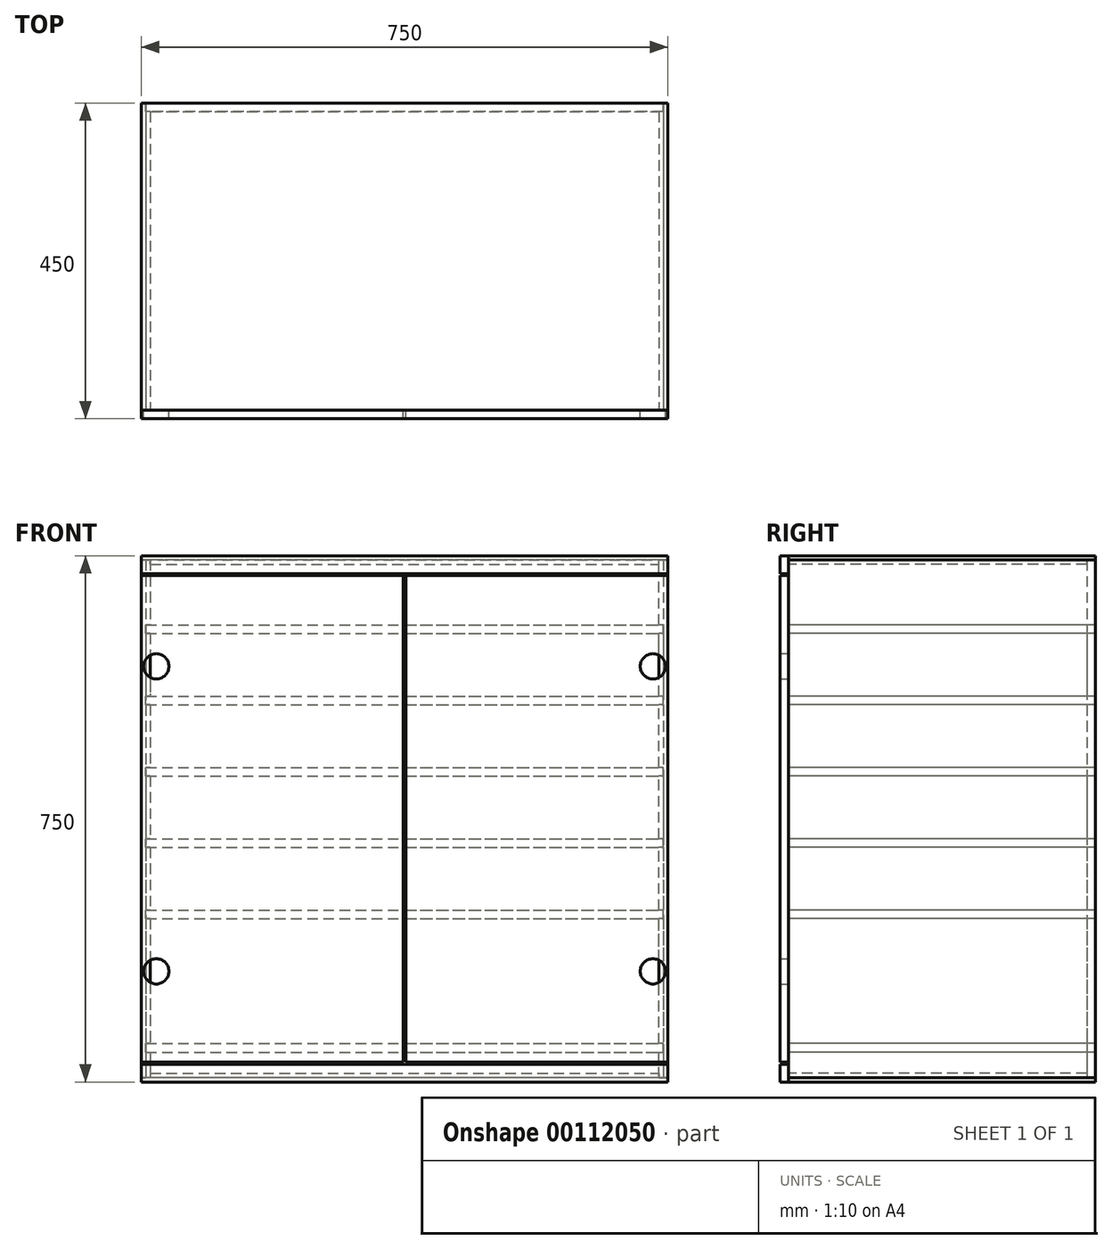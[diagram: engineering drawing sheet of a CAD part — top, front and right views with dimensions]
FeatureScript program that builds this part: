
annotation { "Feature Type Name" : "Feature", "Feature Type Description" : "" }
export const myFeature = defineFeature(function(context is Context, id is Id, definition is map)
    precondition{}
    {
        {
            assignVariable(context, id + "F0", {"name" : "moduleDepth", "anyValue" : 450 * mm});
        }
        {
            assignVariable(context, id + "F1", {"name" : "sideThick", "anyValue" : 12.45 * mm});
        }
        {
            assignVariable(context, id + "F2", {"name" : "backingThick", "anyValue" : getVariable(context, 'sideThick')});
        }
        {
            assignVariable(context, id + "F3", {"name" : "drawerFaceThick", "anyValue" : getVariable(context, 'sideThick')});
        }
        {
            assignVariable(context, id + "F4", {"name" : "drawerCaseDepth", "anyValue" : getVariable(context, 'moduleDepth') - getVariable(context, 'drawerFaceThick')});
        }
        {
            var Q0;
            Q0=qCreatedBy(makeId("Front.planeOp"),FACE);
            var sketch = newSketch(context, id + "F5", { "sketchPlane" : qUnion([Q0])});
            skLineSegment(sketch, "E0.bottom", {"start": v(0, 0) * mm, "end": v(750, 0) * mm});
            skLineSegment(sketch, "E0.top", {"start": v(0, 750) * mm, "end": v(750, 750) * mm});
            skLineSegment(sketch, "E0.left", {"start": v(0, 0) * mm, "end": v(0, 750) * mm});
            skLineSegment(sketch, "E0.right", {"start": v(750, 0) * mm, "end": v(750, 750) * mm});
            skLineSegment(sketch, "E1.bottom", {"start": v(12.45, 12.45) * mm, "end": v(737.55, 12.45) * mm});
            skLineSegment(sketch, "E1.top", {"start": v(12.45, 737.55) * mm, "end": v(737.55, 737.55) * mm});
            skLineSegment(sketch, "E1.left", {"start": v(12.45, 12.45) * mm, "end": v(12.45, 737.55) * mm});
            skLineSegment(sketch, "E1.right", {"start": v(737.55, 12.45) * mm, "end": v(737.55, 737.55) * mm});
            skLineSegment(sketch, "E2", {"start": v(0, 375) * mm, "end": v(750, 375) * mm, "construction": true});
            skLineSegment(sketch, "E3", {"start": v(375, 750) * mm, "end": v(375, 0) * mm, "construction": true});
            skLineSegment(sketch, "E4", {"start": v(12.45, 737.55) * mm, "end": v(12.45, 743.78) * mm});
            skLineSegment(sketch, "E5", {"start": v(12.45, 743.78) * mm, "end": v(0, 743.78) * mm});
            skLineSegment(sketch, "E6.MirrorCS", {"start": v(737.55, 743.78) * mm, "end": v(750, 743.78) * mm});
            skLineSegment(sketch, "E7.MirrorCS", {"start": v(737.55, 737.55) * mm, "end": v(737.55, 743.78) * mm});
            skLineSegment(sketch, "E8.MirrorCS", {"start": v(12.45, 12.45) * mm, "end": v(12.45, 6.22) * mm});
            skLineSegment(sketch, "E9.MirrorCS", {"start": v(737.55, 12.45) * mm, "end": v(737.55, 6.22) * mm});
            skLineSegment(sketch, "E10.MirrorCS", {"start": v(737.55, 6.22) * mm, "end": v(750, 6.22) * mm});
            skLineSegment(sketch, "E11.MirrorCS", {"start": v(12.45, 6.22) * mm, "end": v(0, 6.22) * mm});
            skSolve(sketch);
        }
        {
            var Q0;
            Q0=qCreatedBy(makeId("Front.planeOp"),FACE);
            var sketch = newSketch(context, id + "F6", { "sketchPlane" : qUnion([Q0])});
            skLineSegment(sketch, "E12", {"start": v(6.22, -31.87) * mm, "end": v(6.22, 794) * mm, "construction": true});
            skLineSegment(sketch, "E13", {"start": v(6.22, -31.87) * mm, "end": v(743.78, -31.87) * mm, "construction": true});
            skLineSegment(sketch, "E14", {"start": v(743.78, -31.87) * mm, "end": v(743.78, 794) * mm, "construction": true});
            skLineSegment(sketch, "E15", {"start": v(6.22, 794) * mm, "end": v(743.78, 794) * mm, "construction": true});
            skLineSegment(sketch, "E16.bottom", {"start": v(6.22, 42.45) * mm, "end": v(743.78, 42.45) * mm});
            skLineSegment(sketch, "E16.top", {"start": v(6.22, 54.9) * mm, "end": v(743.78, 54.9) * mm});
            skLineSegment(sketch, "E16.left", {"start": v(6.22, 42.45) * mm, "end": v(6.22, 54.9) * mm});
            skLineSegment(sketch, "E16.right", {"start": v(743.78, 42.45) * mm, "end": v(743.78, 54.9) * mm});
            skLineSegment(sketch, "E17.bottom", {"start": v(6.22, 232.7) * mm, "end": v(743.78, 232.7) * mm});
            skLineSegment(sketch, "E17.top", {"start": v(6.22, 245.14) * mm, "end": v(743.78, 245.14) * mm});
            skLineSegment(sketch, "E17.left", {"start": v(6.22, 232.7) * mm, "end": v(6.22, 245.14) * mm});
            skLineSegment(sketch, "E17.right", {"start": v(743.78, 232.7) * mm, "end": v(743.78, 245.14) * mm});
            skLineSegment(sketch, "E18.0.1.0", {"start": v(6.22, 346.74) * mm, "end": v(743.78, 346.74) * mm});
            skLineSegment(sketch, "E18.0.1.1", {"start": v(6.22, 334.3) * mm, "end": v(743.78, 334.3) * mm});
            skLineSegment(sketch, "E18.0.1.2", {"start": v(743.78, 334.3) * mm, "end": v(743.78, 346.74) * mm});
            skLineSegment(sketch, "E18.0.1.3", {"start": v(6.22, 334.3) * mm, "end": v(6.22, 346.74) * mm});
            skLineSegment(sketch, "E18.0.2.0", {"start": v(6.22, 448.34) * mm, "end": v(743.78, 448.34) * mm});
            skLineSegment(sketch, "E18.0.2.1", {"start": v(6.22, 435.9) * mm, "end": v(743.78, 435.9) * mm});
            skLineSegment(sketch, "E18.0.2.2", {"start": v(743.78, 435.9) * mm, "end": v(743.78, 448.34) * mm});
            skLineSegment(sketch, "E18.0.2.3", {"start": v(6.22, 435.9) * mm, "end": v(6.22, 448.34) * mm});
            skLineSegment(sketch, "E18.0.3.0", {"start": v(6.22, 549.94) * mm, "end": v(743.78, 549.94) * mm});
            skLineSegment(sketch, "E18.0.3.1", {"start": v(6.22, 537.5) * mm, "end": v(743.78, 537.5) * mm});
            skLineSegment(sketch, "E18.0.3.2", {"start": v(743.78, 537.5) * mm, "end": v(743.78, 549.94) * mm});
            skLineSegment(sketch, "E18.0.3.3", {"start": v(6.22, 537.5) * mm, "end": v(6.22, 549.94) * mm});
            skLineSegment(sketch, "E18.0.4.0", {"start": v(6.22, 651.54) * mm, "end": v(743.78, 651.54) * mm});
            skLineSegment(sketch, "E18.0.4.1", {"start": v(6.22, 639.1) * mm, "end": v(743.78, 639.1) * mm});
            skLineSegment(sketch, "E18.0.4.2", {"start": v(743.78, 639.1) * mm, "end": v(743.78, 651.54) * mm});
            skLineSegment(sketch, "E18.0.4.3", {"start": v(6.22, 639.1) * mm, "end": v(6.22, 651.54) * mm});
            skLineSegment(sketch, "E18.direction1", {"start": v(6.22, 232.7) * mm, "end": v(31.22, 232.7) * mm, "construction": true});
            skLineSegment(sketch, "E18.direction2", {"start": v(6.22, 232.7) * mm, "end": v(6.22, 334.3) * mm, "construction": true});
            skSolve(sketch);
        }
        {
            var Q0;
            Q0=qCreatedBy(makeId("Front.planeOp"),FACE);
            var sketch = newSketch(context, id + "F7", { "sketchPlane" : qUnion([Q0])});
            skLineSegment(sketch, "E19.bottom", {"start": v(0, 0) * mm, "end": v(750, 0) * mm});
            skLineSegment(sketch, "E19.top", {"start": v(0, 25.4) * mm, "end": v(750, 25.4) * mm});
            skLineSegment(sketch, "E19.left", {"start": v(0, 0) * mm, "end": v(0, 25.4) * mm});
            skLineSegment(sketch, "E19.right", {"start": v(750, 0) * mm, "end": v(750, 25.4) * mm});
            skLineSegment(sketch, "E20.MirrorCS", {"start": v(0, 750) * mm, "end": v(0, 724.6) * mm});
            skLineSegment(sketch, "E21.MirrorCS", {"start": v(750, 750) * mm, "end": v(750, 724.6) * mm});
            skLineSegment(sketch, "E22.MirrorCS", {"start": v(0, 724.6) * mm, "end": v(750, 724.6) * mm});
            skLineSegment(sketch, "E23.MirrorCS", {"start": v(0, 750) * mm, "end": v(750, 750) * mm});
            skLineSegment(sketch, "E24.bottom", {"start": v(0, 28.4) * mm, "end": v(373, 28.4) * mm});
            skLineSegment(sketch, "E24.top", {"start": v(0, 721.6) * mm, "end": v(373, 721.6) * mm});
            skLineSegment(sketch, "E24.left", {"start": v(0, 28.4) * mm, "end": v(0, 721.6) * mm});
            skLineSegment(sketch, "E24.right", {"start": v(373, 28.4) * mm, "end": v(373, 721.6) * mm});
            skLineSegment(sketch, "E25.MirrorCS", {"start": v(377, 28.4) * mm, "end": v(377, 721.6) * mm});
            skLineSegment(sketch, "E26.MirrorCS", {"start": v(750, 28.4) * mm, "end": v(750, 721.6) * mm});
            skLineSegment(sketch, "E27.MirrorCS", {"start": v(750, 721.6) * mm, "end": v(377, 721.6) * mm});
            skLineSegment(sketch, "E28.MirrorCS", {"start": v(750, 28.4) * mm, "end": v(377, 28.4) * mm});
            skCircle(sketch, "E29", {"center": v(21, 157.66) * mm, "radius": 18 * mm});
            skLineSegment(sketch, "E30", {"start": v(7.58, 145.66) * mm, "end": v(34.42, 145.66) * mm});
            skLineSegment(sketch, "E31", {"start": v(34.42, 145.66) * mm, "end": v(34.42, 169.66) * mm, "construction": true});
            skLineSegment(sketch, "E32", {"start": v(34.42, 169.66) * mm, "end": v(7.58, 169.66) * mm});
            skCircle(sketch, "E33.MirrorC", {"center": v(729, 157.66) * mm, "radius": 18 * mm});
            skLineSegment(sketch, "E34.MirrorCS", {"start": v(715.58, 145.66) * mm, "end": v(715.58, 169.66) * mm, "construction": true});
            skLineSegment(sketch, "E35.MirrorCS", {"start": v(742.42, 145.66) * mm, "end": v(715.58, 145.66) * mm});
            skLineSegment(sketch, "E36.MirrorCS", {"start": v(715.58, 169.66) * mm, "end": v(742.42, 169.66) * mm});
            skLineSegment(sketch, "E37.MirrorCS", {"start": v(34.42, 580.34) * mm, "end": v(7.58, 580.34) * mm});
            skLineSegment(sketch, "E38.MirrorCS", {"start": v(742.42, 604.34) * mm, "end": v(715.58, 604.34) * mm});
            skLineSegment(sketch, "E39.MirrorCS", {"start": v(715.58, 580.34) * mm, "end": v(742.42, 580.34) * mm});
            skLineSegment(sketch, "E40.MirrorCS", {"start": v(7.58, 604.34) * mm, "end": v(34.42, 604.34) * mm});
            skLineSegment(sketch, "E41.MirrorCS", {"start": v(34.42, 604.34) * mm, "end": v(34.42, 580.34) * mm, "construction": true});
            skLineSegment(sketch, "E42.MirrorCS", {"start": v(715.58, 604.34) * mm, "end": v(715.58, 580.34) * mm, "construction": true});
            skCircle(sketch, "E43.MirrorC", {"center": v(729, 592.34) * mm, "radius": 18 * mm});
            skCircle(sketch, "E44.MirrorC", {"center": v(21, 592.34) * mm, "radius": 18 * mm});
            skSolve(sketch);
        }
        {
            var Q0;
            {var subQ1=sQuery(id+"F5.wireOp",EDGE,"E0.top");Q0=makeQuery(id+"F5.imprint","IMPRINT",FACE,{"disambiguationData":[TD([[makeQuery(id+"F5.imprint","IMPRINT",EDGE,{"derivedFrom":subQ1}),-1.0]])]});}
            var Q1;
            {var subQ1=sQuery(id+"F5.wireOp",EDGE,"E0.bottom");Q1=makeQuery(id+"F5.imprint","IMPRINT",FACE,{"disambiguationData":[TD([[makeQuery(id+"F5.imprint","IMPRINT",EDGE,{"derivedFrom":subQ1}),1.0]])]});}
            extrude(context, id + "F8", {"entities" : qUnion([Q0, Q1]), "oppositeDirection" : true, "depth" : getVariable(context, 'drawerCaseDepth')});
        }
        {
            var Q0;
            Q0=makeQuery(id+"F5.imprint","IMPRINT",FACE,{"disambiguationData":[TD([[makeQuery(id+"F5.imprint","IMPRINT",EDGE,{"derivedFrom":sQuery(id+"F5.wireOp",EDGE,"E1.left")}),1.0]])]});
            var Q1;
            Q1=makeQuery(id+"F5.imprint","IMPRINT",FACE,{"disambiguationData":[TD([[makeQuery(id+"F5.imprint","IMPRINT",EDGE,{"derivedFrom":sQuery(id+"F5.wireOp",EDGE,"E1.right")}),-1.0]])]});
            var Q2;
            Q2=makeQuery(id+"F8.opExtrude","CAP_FACE",FACE,{"disambiguationData":[OSD([sQuery(id+"F5.wireOp",EDGE,"E0.top"),sQuery(id+"F5.wireOp",EDGE,"E0.left"),sQuery(id+"F5.wireOp",EDGE,"E0.right"),sQuery(id+"F5.wireOp",EDGE,"E1.top"),sQuery(id+"F5.wireOp",EDGE,"E4"),sQuery(id+"F5.wireOp",EDGE,"E5"),sQuery(id+"F5.wireOp",EDGE,"E6.MirrorCS"),sQuery(id+"F5.wireOp",EDGE,"E7.MirrorCS")])],"isStart":false});
            var Q3;
            Q3=makeQuery(id+"F8.opExtrude","CAP_FACE",FACE,{"disambiguationData":[OSD([sQuery(id+"F5.wireOp",EDGE,"E0.top"),sQuery(id+"F5.wireOp",EDGE,"E0.left"),sQuery(id+"F5.wireOp",EDGE,"E0.right"),sQuery(id+"F5.wireOp",EDGE,"E1.top"),sQuery(id+"F5.wireOp",EDGE,"E4"),sQuery(id+"F5.wireOp",EDGE,"E5"),sQuery(id+"F5.wireOp",EDGE,"E6.MirrorCS"),sQuery(id+"F5.wireOp",EDGE,"E7.MirrorCS")])],"isStart":true});
            extrude(context, id + "F9", {"entities" : qUnion([Q0, Q1]), "endBound" : BoundingType.UP_TO_SURFACE, "oppositeDirection" : true, "endBoundEntityFace" : qUnion([Q2]), "depth" : 25.4 * mm});
        }
        {
            var Q0;
            Q0=makeQuery(id+"F8.opExtrude","CAP_FACE",FACE,{"disambiguationData":[OSD([sQuery(id+"F5.wireOp",EDGE,"E0.top"),sQuery(id+"F5.wireOp",EDGE,"E0.left"),sQuery(id+"F5.wireOp",EDGE,"E0.right"),sQuery(id+"F5.wireOp",EDGE,"E1.top"),sQuery(id+"F5.wireOp",EDGE,"E4"),sQuery(id+"F5.wireOp",EDGE,"E5"),sQuery(id+"F5.wireOp",EDGE,"E6.MirrorCS"),sQuery(id+"F5.wireOp",EDGE,"E7.MirrorCS")])],"isStart":false});
            var sketch = newSketch(context, id + "F10", { "sketchPlane" : qUnion([Q0])});
            skLineSegment(sketch, "E45.bottom", {"start": v(-743.78, 743.78) * mm, "end": v(-6.22, 743.78) * mm});
            skLineSegment(sketch, "E45.top", {"start": v(-743.78, 6.22) * mm, "end": v(-6.22, 6.22) * mm});
            skLineSegment(sketch, "E45.left", {"start": v(-743.78, 743.78) * mm, "end": v(-743.78, 6.22) * mm});
            skLineSegment(sketch, "E45.right", {"start": v(-6.22, 743.78) * mm, "end": v(-6.22, 6.22) * mm});
            skSolve(sketch);
        }
        {
            var Q0;
            Q0=qSketchRegion(id+"F10",true);
            extrude(context, id + "F11", {"entities" : qUnion([Q0]), "oppositeDirection" : true, "depth" : getVariable(context, 'backingThick')});
        }
        {
            var Q0;
            Q0=makeQuery(id+"F11.opExtrude","SWEPT_BODY",BODY,{"disambiguationData":[OSD([sQuery(id+"F10.wireOp",EDGE,"E45.bottom"),sQuery(id+"F10.wireOp",EDGE,"E45.top"),sQuery(id+"F10.wireOp",EDGE,"E45.left"),sQuery(id+"F10.wireOp",EDGE,"E45.right")])]});
            var Q1;
            Q1=makeQuery(id+"F8.opExtrude","SWEPT_BODY",BODY,{"disambiguationData":[OSD([sQuery(id+"F5.wireOp",EDGE,"E0.top"),sQuery(id+"F5.wireOp",EDGE,"E0.left"),sQuery(id+"F5.wireOp",EDGE,"E0.right"),sQuery(id+"F5.wireOp",EDGE,"E1.top"),sQuery(id+"F5.wireOp",EDGE,"E4"),sQuery(id+"F5.wireOp",EDGE,"E5"),sQuery(id+"F5.wireOp",EDGE,"E6.MirrorCS"),sQuery(id+"F5.wireOp",EDGE,"E7.MirrorCS")])]});
            var Q2;
            Q2=makeQuery(id+"F9.opExtrude","SWEPT_BODY",BODY,{"disambiguationData":[OSD([sQuery(id+"F5.wireOp",EDGE,"E0.right"),sQuery(id+"F5.wireOp",EDGE,"E1.right"),sQuery(id+"F5.wireOp",EDGE,"E6.MirrorCS"),sQuery(id+"F5.wireOp",EDGE,"E7.MirrorCS"),sQuery(id+"F5.wireOp",EDGE,"E9.MirrorCS"),sQuery(id+"F5.wireOp",EDGE,"E10.MirrorCS")])]});
            var Q3;
            Q3=makeQuery(id+"F9.opExtrude","SWEPT_BODY",BODY,{"disambiguationData":[OSD([sQuery(id+"F5.wireOp",EDGE,"E0.left"),sQuery(id+"F5.wireOp",EDGE,"E1.left"),sQuery(id+"F5.wireOp",EDGE,"E4"),sQuery(id+"F5.wireOp",EDGE,"E5"),sQuery(id+"F5.wireOp",EDGE,"E8.MirrorCS"),sQuery(id+"F5.wireOp",EDGE,"E11.MirrorCS")])]});
            var Q4;
            Q4=makeQuery(id+"F8.opExtrude","SWEPT_BODY",BODY,{"disambiguationData":[OSD([sQuery(id+"F5.wireOp",EDGE,"E0.bottom"),sQuery(id+"F5.wireOp",EDGE,"E0.left"),sQuery(id+"F5.wireOp",EDGE,"E0.right"),sQuery(id+"F5.wireOp",EDGE,"E1.bottom"),sQuery(id+"F5.wireOp",EDGE,"E8.MirrorCS"),sQuery(id+"F5.wireOp",EDGE,"E9.MirrorCS"),sQuery(id+"F5.wireOp",EDGE,"E10.MirrorCS"),sQuery(id+"F5.wireOp",EDGE,"E11.MirrorCS")])]});
            booleanBodies(context, id + "F12", {"operationType" : BooleanOperationType.SUBTRACTION, "tools" : qUnion([Q0]), "targets" : qUnion([Q1, Q2, Q3, Q4]), "keepTools" : true});
        }
        {
            var Q0;
            Q0 = qSketchRegion(id + "F6", true);
            extrude(context, id + "F13", {"entities" : qUnion([Q0]), "oppositeDirection" : true, "depth" : getVariable(context, 'moduleDepth') - getVariable(context, 'sideThick')});
        }
        {
            var Q0;
            Q0=makeQuery(id+"F13.opExtrude","SWEPT_BODY",BODY,{"disambiguationData":[OSD([sQuery(id+"F6.wireOp",EDGE,"E18.0.4.0"),sQuery(id+"F6.wireOp",EDGE,"E18.0.4.1"),sQuery(id+"F6.wireOp",EDGE,"E18.0.4.2"),sQuery(id+"F6.wireOp",EDGE,"E18.0.4.3")])]});
            var Q1;
            Q1=makeQuery(id+"F13.opExtrude","SWEPT_BODY",BODY,{"disambiguationData":[OSD([sQuery(id+"F6.wireOp",EDGE,"E18.0.3.0"),sQuery(id+"F6.wireOp",EDGE,"E18.0.3.1"),sQuery(id+"F6.wireOp",EDGE,"E18.0.3.2"),sQuery(id+"F6.wireOp",EDGE,"E18.0.3.3")])]});
            var Q2;
            Q2=makeQuery(id+"F13.opExtrude","SWEPT_BODY",BODY,{"disambiguationData":[OSD([sQuery(id+"F6.wireOp",EDGE,"E18.0.2.0"),sQuery(id+"F6.wireOp",EDGE,"E18.0.2.1"),sQuery(id+"F6.wireOp",EDGE,"E18.0.2.2"),sQuery(id+"F6.wireOp",EDGE,"E18.0.2.3")])]});
            var Q3;
            Q3=makeQuery(id+"F13.opExtrude","SWEPT_BODY",BODY,{"disambiguationData":[OSD([sQuery(id+"F6.wireOp",EDGE,"E18.0.1.0"),sQuery(id+"F6.wireOp",EDGE,"E18.0.1.1"),sQuery(id+"F6.wireOp",EDGE,"E18.0.1.2"),sQuery(id+"F6.wireOp",EDGE,"E18.0.1.3")])]});
            var Q4;
            Q4=makeQuery(id+"F13.opExtrude","SWEPT_BODY",BODY,{"disambiguationData":[OSD([sQuery(id+"F6.wireOp",EDGE,"E17.bottom"),sQuery(id+"F6.wireOp",EDGE,"E17.top"),sQuery(id+"F6.wireOp",EDGE,"E17.left"),sQuery(id+"F6.wireOp",EDGE,"E17.right")])]});
            var Q5;
            Q5=makeQuery(id+"F13.opExtrude","SWEPT_BODY",BODY,{"disambiguationData":[OSD([sQuery(id+"F6.wireOp",EDGE,"E16.bottom"),sQuery(id+"F6.wireOp",EDGE,"E16.top"),sQuery(id+"F6.wireOp",EDGE,"E16.left"),sQuery(id+"F6.wireOp",EDGE,"E16.right")])]});
            var Q6;
            Q6=makeQuery(id+"F9.opExtrude","SWEPT_BODY",BODY,{"disambiguationData":[OSD([sQuery(id+"F5.wireOp",EDGE,"E0.left"),sQuery(id+"F5.wireOp",EDGE,"E1.left"),sQuery(id+"F5.wireOp",EDGE,"E4"),sQuery(id+"F5.wireOp",EDGE,"E5"),sQuery(id+"F5.wireOp",EDGE,"E8.MirrorCS"),sQuery(id+"F5.wireOp",EDGE,"E11.MirrorCS")])]});
            var Q7;
            Q7=makeQuery(id+"F9.opExtrude","SWEPT_BODY",BODY,{"disambiguationData":[OSD([sQuery(id+"F5.wireOp",EDGE,"E0.right"),sQuery(id+"F5.wireOp",EDGE,"E1.right"),sQuery(id+"F5.wireOp",EDGE,"E6.MirrorCS"),sQuery(id+"F5.wireOp",EDGE,"E7.MirrorCS"),sQuery(id+"F5.wireOp",EDGE,"E9.MirrorCS"),sQuery(id+"F5.wireOp",EDGE,"E10.MirrorCS")])]});
            booleanBodies(context, id + "F14", {"operationType" : BooleanOperationType.SUBTRACTION, "tools" : qUnion([Q0, Q1, Q2, Q3, Q4, Q5]), "targets" : qUnion([Q6, Q7]), "keepTools" : true});
        }
        {
            var Q0;
            Q0 = qSketchRegion(id + "F7", true);
            extrude(context, id + "F15", {"entities" : qUnion([Q0]), "depth" : getVariable(context, 'sideThick')});
        }
    });
